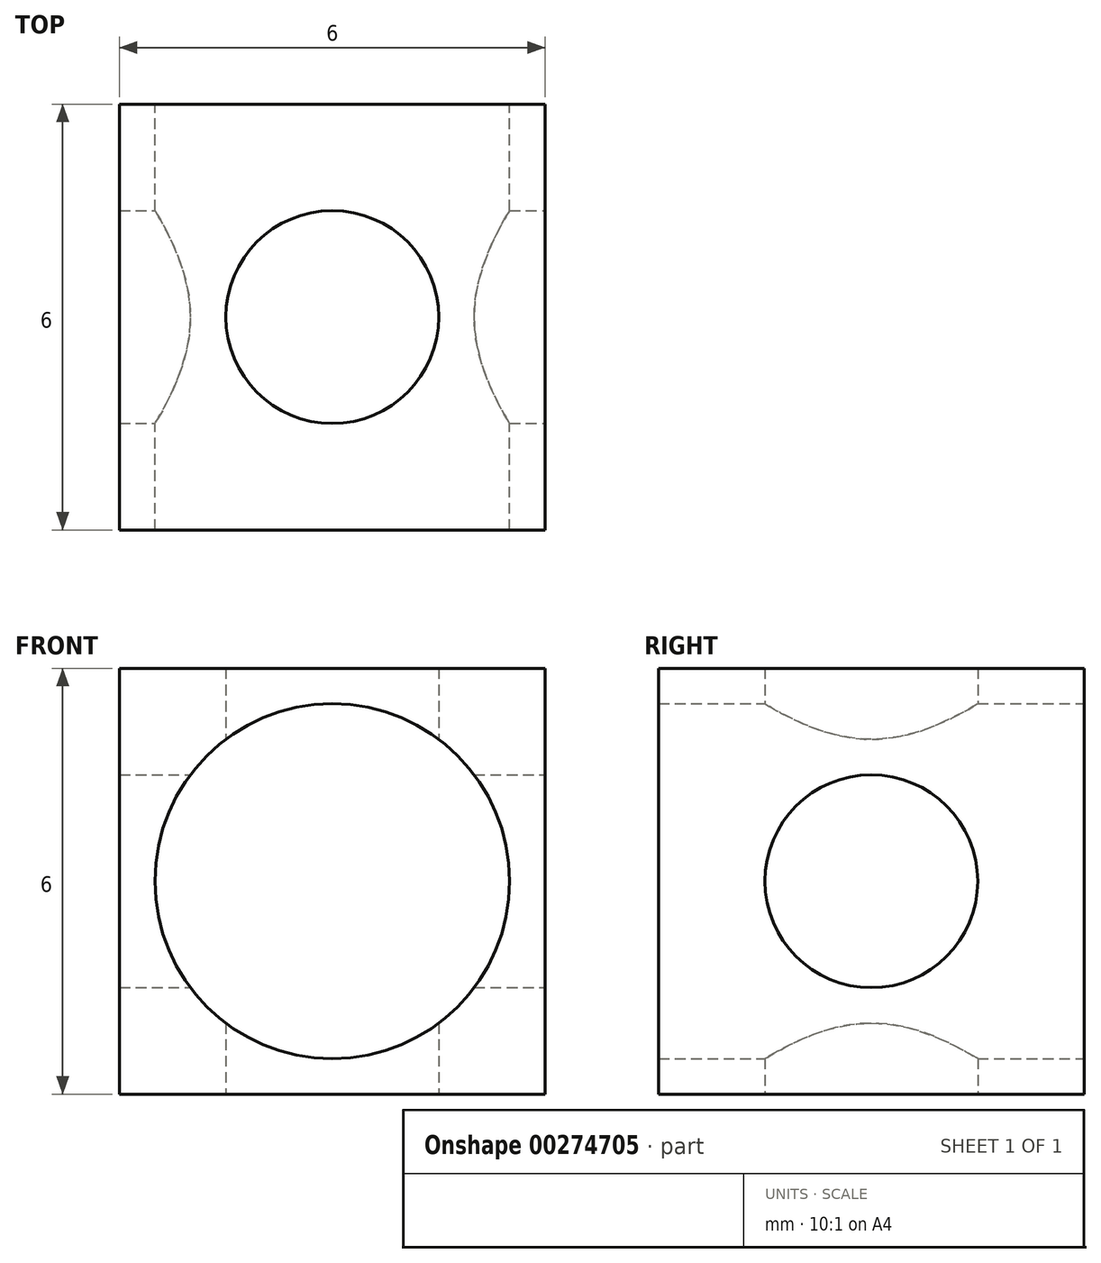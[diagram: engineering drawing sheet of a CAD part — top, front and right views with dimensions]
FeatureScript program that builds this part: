
annotation { "Feature Type Name" : "Feature", "Feature Type Description" : "" }
export const myFeature = defineFeature(function(context is Context, id is Id, definition is map)
    precondition{}
    {
        {
            var Q0;
            Q0=qCreatedBy(makeId("Top.planeOp"),FACE);
            var sketch = newSketch(context, id + "F0", { "sketchPlane" : qUnion([Q0])});
            skLineSegment(sketch, "E0.bottom", {"start": v(-3, -3) * mm, "end": v(3, -3) * mm});
            skLineSegment(sketch, "E0.top", {"start": v(-3, 3) * mm, "end": v(3, 3) * mm});
            skLineSegment(sketch, "E0.left", {"start": v(-3, -3) * mm, "end": v(-3, 3) * mm});
            skLineSegment(sketch, "E0.right", {"start": v(3, -3) * mm, "end": v(3, 3) * mm});
            skPoint(sketch, "E0.middle", {"position": v(0, 0) * mm});
            skCircle(sketch, "E1", {"center": v(0, 0) * mm, "radius": 1.5 * mm});
            skSolve(sketch);
        }
        {
            var Q0;
            Q0 = qSketchRegion(id + "F0", true);
            extrude(context, id + "F1", {"entities" : qUnion([Q0]), "depth" : 6 * mm});
        }
        {
            var Q0;
            Q0=makeQuery(id+"F1.opExtrude","SWEPT_FACE",FACE,{"disambiguationData":[OSD([sQuery(id+"F0.wireOp",EDGE,"E0.right")])]});
            var sketch = newSketch(context, id + "F2", { "sketchPlane" : qUnion([Q0])});
            skCircle(sketch, "E2", {"center": v(0, 3) * mm, "radius": 1.5 * mm});
            skPoint(sketch, "E2.centerSnap0", {"position": v(-3, 3) * mm});
            skPoint(sketch, "E2.centerSnap1", {"position": v(0, 6) * mm});
            skSolve(sketch);
        }
        {
            var Q0;
            Q0 = qSketchRegion(id + "F2", true);
            extrude(context, id + "F3", {"entities" : qUnion([Q0]), "operationType" : NewBodyOperationType.REMOVE, "oppositeDirection" : true, "depth" : 25 * mm});
        }
        {
            var Q0;
            Q0=makeQuery(id+"F1.opExtrude","SWEPT_FACE",FACE,{"disambiguationData":[OSD([sQuery(id+"F0.wireOp",EDGE,"E0.top")])]});
            var sketch = newSketch(context, id + "F4", { "sketchPlane" : qUnion([Q0])});
            skCircle(sketch, "E3", {"center": v(0, 3) * mm, "radius": 2.5 * mm});
            skPoint(sketch, "E3.centerSnap0", {"position": v(0, 6) * mm});
            skPoint(sketch, "E3.centerSnap1", {"position": v(-3, 3) * mm});
            skSolve(sketch);
        }
        {
            var Q0;
            Q0 = qSketchRegion(id + "F4", true);
            extrude(context, id + "F5", {"entities" : qUnion([Q0]), "operationType" : NewBodyOperationType.REMOVE, "oppositeDirection" : true, "depth" : 25 * mm});
        }
    });
